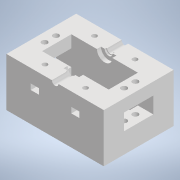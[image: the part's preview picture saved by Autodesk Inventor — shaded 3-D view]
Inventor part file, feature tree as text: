
AUTODESK INVENTOR PART (.ipt)
format: ipt  version: 2020.2 (Build 242310000, 310)  size: 381,440 bytes
history: native  units: mm
features: sketch x15, extrude x13, other x3, hole x2, reference x1
ambient origin geometry x8: Origin, YZ Plane, XZ Plane, XY Plane, X Axis, Y Axis, Z Axis, Center Point
bodies: Solido1 (feature_tree)
feature tree (34):
  extrude  "Estrusione1"  Depth=120.0mm
  extrude  "Estrusione2"  Depth=86.0mm
  extrude  "Estrusione3"  Depth=60.0mm TaperAngle=0.0deg
  extrude  "Estrusione4"  Depth=15.0mm
  extrude  "Estrusione5"  Depth=36.0mm
  extrude  "Estrusione6"  Depth=30.0mm
  hole  "Foro1"  [1 undecoded]
  extrude  "Estrusione7"  Depth=19.0mm
  extrude  "Estrusione8"  Depth=5.0mm TaperAngle=0.0deg
  sketch  "Schizzo12"
  extrude  "Estrusione9"  Depth=8.0mm
  extrude  "Estrusione11"  Depth=20.0mm TaperAngle=0.0deg
  extrude  "Estrusione12"  Depth=19.0mm
  extrude  "Estrusione14"  Depth=5.0mm TaperAngle=0.0deg
  hole  "Foro5"  [1 undecoded]
  extrude  "Estrusione15"  Depth=50.0mm
  sketch  "Schizzo1"
  sketch  "Schizzo2"
  sketch  "Schizzo3"
  sketch  "Schizzo4"
  sketch  "Schizzo5"
  sketch  "Schizzo6"
  sketch  "Schizzo7"
  sketch  "Schizzo8"
  sketch  "Schizzo10"
  sketch  "Schizzo13"
  sketch  "Schizzo16"
  sketch  "Schizzo17"
  sketch  "Schizzo21"
  sketch  "Schizzo22"
  reference  "Riferimento1"
  other  "<userpath>\Desktop\mv-Project\04_PartDraw\Pendolo_Inverso.iam"
  other  "Pendolo_Inverso.iam"
  other  "20_Base_Sopra:2"
note: 2 required parameter values undecoded (feature->parameter linkage not recoverable at this tier; creation-order binding heuristic only, values carry confidence <= 0.55)
